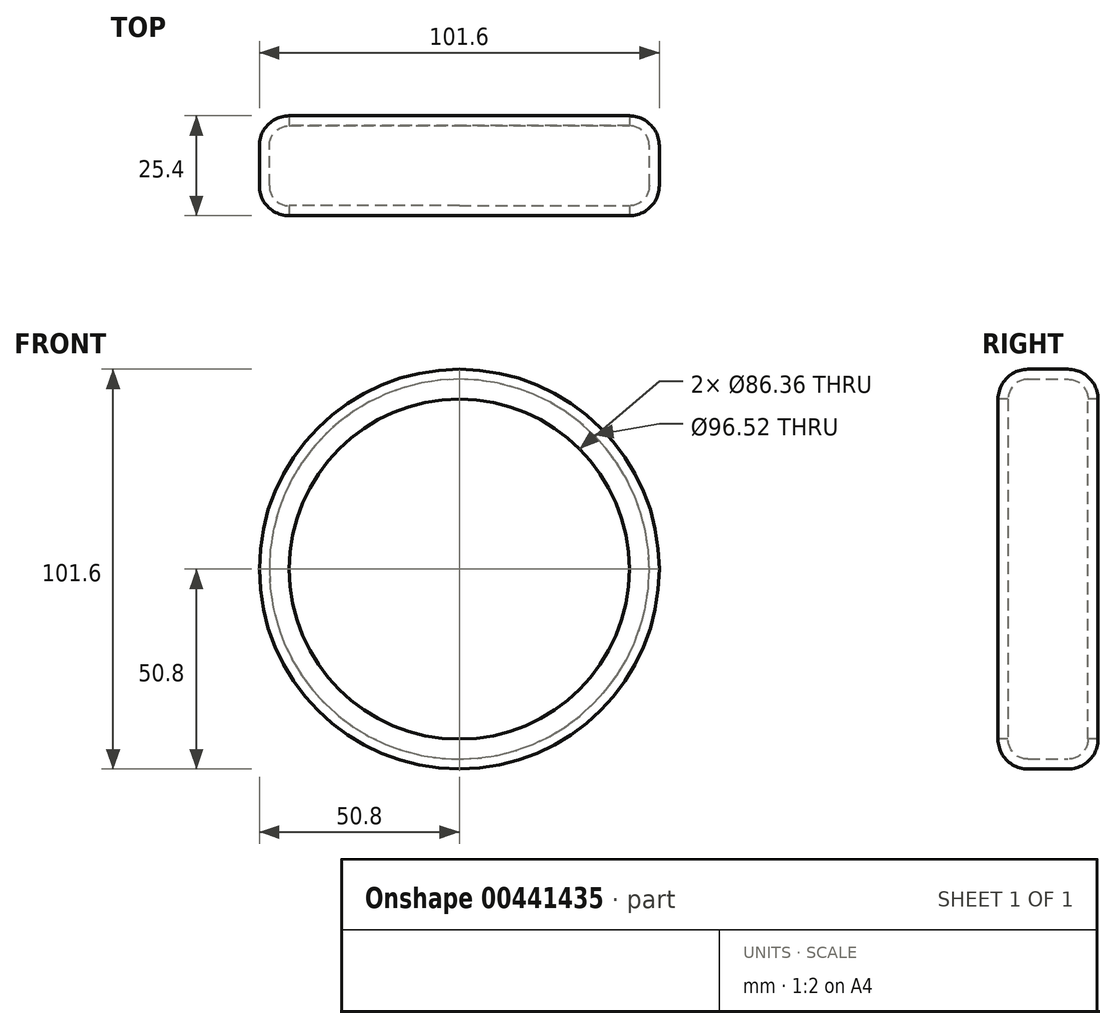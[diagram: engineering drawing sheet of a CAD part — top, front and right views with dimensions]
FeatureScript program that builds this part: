
annotation { "Feature Type Name" : "Feature", "Feature Type Description" : "" }
export const myFeature = defineFeature(function(context is Context, id is Id, definition is map)
    precondition{}
    {
        {
            var Q0;
            Q0=qCreatedBy(makeId("Front.planeOp"),FACE);
            var sketch = newSketch(context, id + "F0", { "sketchPlane" : qUnion([Q0])});
            skCircle(sketch, "E0", {"center": v(0, 0) * mm, "radius": 50.8 * mm});
            skSolve(sketch);
        }
        {
            var Q0;
            Q0 = qSketchRegion(id + "F0", true);
            extrude(context, id + "F1", {"entities" : qUnion([Q0]), "depth" : 25.4 * mm});
        }
        {
            var Q0;
            Q0=makeQuery(id+"F1.opExtrude","CAP_EDGE",EDGE,{"disambiguationData":[OSD([sQuery(id+"F0.wireOp",EDGE,"E0")])],"isStart":false});
            var Q1;
            Q1=makeQuery(id+"F1.opExtrude","CAP_EDGE",EDGE,{"disambiguationData":[OSD([sQuery(id+"F0.wireOp",EDGE,"E0")])],"isStart":true});
            fillet(context, id + "F2", {"entities" : qUnion([Q0, Q1]), "radius" : 7.62 * mm, "tangentPropagation" : true, "allowEdgeOverflow" : false});
        }
        {
            var Q0;
            Q0=makeQuery(id+"F1.opExtrude","CAP_FACE",FACE,{"disambiguationData":[OSD([sQuery(id+"F0.wireOp",EDGE,"E0")])],"isStart":false});
            var Q1;
            Q1=makeQuery(id+"F1.opExtrude","CAP_FACE",FACE,{"disambiguationData":[OSD([sQuery(id+"F0.wireOp",EDGE,"E0")])],"isStart":true});
            shell(context, id + "F3", {"entities" : qUnion([Q0, Q1]), "thickness" : 2.54 * mm});
        }
    });
